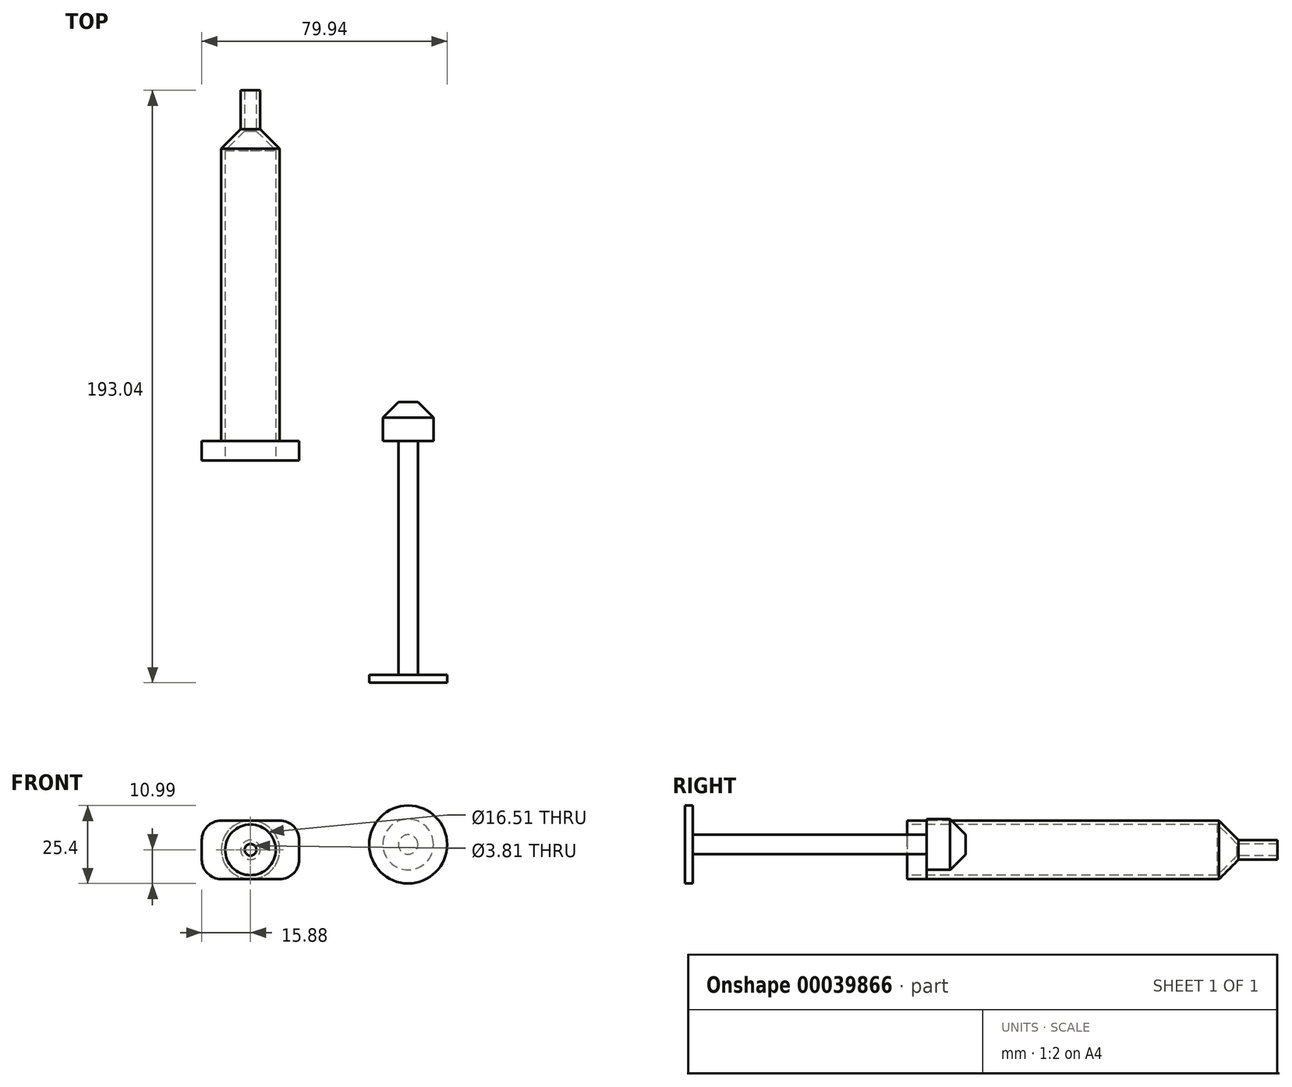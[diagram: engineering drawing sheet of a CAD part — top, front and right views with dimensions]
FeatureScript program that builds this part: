
annotation { "Feature Type Name" : "Feature", "Feature Type Description" : "" }
export const myFeature = defineFeature(function(context is Context, id is Id, definition is map)
    precondition{}
    {
        {
            var Q0;
            Q0=qCreatedBy(makeId("Front.planeOp"),FACE);
            var sketch = newSketch(context, id + "F0", { "sketchPlane" : qUnion([Q0])});
            skCircle(sketch, "E0", {"center": v(0, 0) * mm, "radius": 9.53 * mm});
            skSolve(sketch);
        }
        {
            var Q0;
            Q0 = qSketchRegion(id + "F0", true);
            extrude(context, id + "F1", {"entities" : qUnion([Q0]), "oppositeDirection" : true, "depth" : 101.6 * mm});
        }
        {
            var Q0;
            Q0=makeQuery(id+"F1.opExtrude","CAP_EDGE",EDGE,{"disambiguationData":[OSD([sQuery(id+"F0.wireOp",EDGE,"E0")])],"isStart":false});
            chamfer(context, id + "F2", {"entities" : qUnion([Q0]), "width" : 6.35 * mm, "tangentPropagation" : true});
        }
        {
            var Q0;
            Q0=makeQuery(id+"F1.opExtrude","CAP_FACE",FACE,{"disambiguationData":[OSD([sQuery(id+"F0.wireOp",EDGE,"E0")])],"isStart":false});
            extrude(context, id + "F3", {"entities" : qUnion([Q0]), "operationType" : NewBodyOperationType.ADD, "depth" : 12.7 * mm});
        }
        {
            var Q0;
            Q0=makeQuery(id+"F1.opExtrude","CAP_FACE",FACE,{"disambiguationData":[OSD([sQuery(id+"F0.wireOp",EDGE,"E0")])],"isStart":true});
            shell(context, id + "F4", {"entities" : qUnion([Q0]), "thickness" : 1.27 * mm});
        }
        {
            var Q0;
            {var subQ0=sQuery(id+"F0.wireOp",EDGE,"E0");Q0=makeQuery(id+"F4.opShell","OFFSET_FACE",FACE,{"disambiguationData":[OSD([subQ0]),TDD([makeQuery(id+"F3.opExtrude","CAP_FACE",FACE,{"disambiguationData":[OSD([subQ0])],"isStart":false})])]});}
            extrude(context, id + "F5", {"entities" : qUnion([Q0]), "operationType" : NewBodyOperationType.REMOVE, "oppositeDirection" : true, "depth" : 25.4 * mm});
        }
        {
            var Q0;
            Q0=makeQuery(id+"F1.opExtrude","CAP_FACE",FACE,{"disambiguationData":[OSD([sQuery(id+"F0.wireOp",EDGE,"E0")])],"isStart":true});
            var sketch = newSketch(context, id + "F6", { "sketchPlane" : qUnion([Q0])});
            skLineSegment(sketch, "E1.rect.bottom", {"start": v(-15.88, 9.52) * mm, "end": v(15.88, 9.52) * mm});
            skLineSegment(sketch, "E1.rect.top", {"start": v(-15.88, -9.53) * mm, "end": v(15.88, -9.53) * mm});
            skLineSegment(sketch, "E1.rect.left", {"start": v(-15.88, 9.52) * mm, "end": v(-15.88, -9.53) * mm});
            skLineSegment(sketch, "E1.rect.right", {"start": v(15.88, 9.52) * mm, "end": v(15.88, -9.53) * mm});
            skPoint(sketch, "E1.rect.middle", {"position": v(0, 0) * mm});
            skSolve(sketch);
        }
        {
            var Q0;
            {var subQ5=sQuery(id+"F6.wireOp",EDGE,"E1.rect.left");Q0=makeQuery(id+"F6.imprint","IMPRINT",FACE,{"disambiguationData":[TD([[makeQuery(id+"F6.imprint","IMPRINT",EDGE,{"derivedFrom":subQ5}),1.0]])]});}
            var Q1;
            {var subQ5=sQuery(id+"F6.wireOp",EDGE,"E1.rect.right");Q1=makeQuery(id+"F6.imprint","IMPRINT",FACE,{"disambiguationData":[TD([[makeQuery(id+"F6.imprint","IMPRINT",EDGE,{"derivedFrom":subQ5}),-1.0]])]});}
            var Q2;
            {var subQ0=sQuery(id+"F0.wireOp",EDGE,"E0");var subQ1=makeQuery(id+"F1.opExtrude","CAP_EDGE",EDGE,{"disambiguationData":[OSD([subQ0])],"isStart":true});Q2=makeQuery(id+"F6.imprint","IMPRINT",FACE,{"disambiguationData":[TD([[makeQuery(id+"F6.imprint","IMPRINT",EDGE,{"derivedFrom":makeQuery(id+"F4.opShell","OFFSET_EDGE",EDGE,{"disambiguationData":[OSD([subQ0]),TDD([subQ1])]})}),-1.0]])]});}
            extrude(context, id + "F7", {"entities" : qUnion([Q0, Q1, Q2]), "operationType" : NewBodyOperationType.ADD, "depth" : 6.35 * mm});
        }
        {
            var Q0;
            Q0=makeQuery(id+"F7.opExtrude","SWEPT_EDGE",EDGE,{"disambiguationData":[OSD([sQuery(id+"F6.wireOp",EDGE,"E1.rect.bottom"),sQuery(id+"F6.wireOp",EDGE,"E1.rect.left")])]});
            var Q1;
            Q1=makeQuery(id+"F7.opExtrude","SWEPT_EDGE",EDGE,{"disambiguationData":[OSD([sQuery(id+"F6.wireOp",EDGE,"E1.rect.bottom"),sQuery(id+"F6.wireOp",EDGE,"E1.rect.right")])]});
            var Q2;
            Q2=makeQuery(id+"F7.opExtrude","SWEPT_EDGE",EDGE,{"disambiguationData":[OSD([sQuery(id+"F6.wireOp",EDGE,"E1.rect.top"),sQuery(id+"F6.wireOp",EDGE,"E1.rect.left")])]});
            var Q3;
            Q3=makeQuery(id+"F7.opExtrude","SWEPT_EDGE",EDGE,{"disambiguationData":[OSD([sQuery(id+"F6.wireOp",EDGE,"E1.rect.top"),sQuery(id+"F6.wireOp",EDGE,"E1.rect.right")])]});
            fillet(context, id + "F8", {"entities" : qUnion([Q0, Q1, Q2, Q3]), "radius" : 6.35 * mm, "tangentPropagation" : true, "allowEdgeOverflow" : false});
        }
        {
            var Q0;
            Q0=qCreatedBy(makeId("Front.planeOp"),FACE);
            var sketch = newSketch(context, id + "F9", { "sketchPlane" : qUnion([Q0])});
            skCircle(sketch, "E2", {"center": v(51.36, 1.71) * mm, "radius": 8.26 * mm});
            skSolve(sketch);
        }
        {
            var Q0;
            Q0=makeQuery(id+"F9.imprint","IMPRINT",FACE,{"disambiguationData":[TD([[makeQuery(id+"F9.imprint","IMPRINT",EDGE,{"derivedFrom":sQuery(id+"F9.wireOp",EDGE,"E2")}),1.0]])]});
            extrude(context, id + "F10", {"entities" : qUnion([Q0]), "oppositeDirection" : true, "depth" : 12.7 * mm});
        }
        {
            var Q0;
            Q0=makeQuery(id+"F10.opExtrude","CAP_FACE",FACE,{"disambiguationData":[OSD([sQuery(id+"F9.wireOp",EDGE,"E2")])],"isStart":true});
            var sketch = newSketch(context, id + "F11", { "sketchPlane" : qUnion([Q0])});
            skCircle(sketch, "E3", {"center": v(51.36, 1.71) * mm, "radius": 3.18 * mm});
            skSolve(sketch);
        }
        {
            var Q0;
            Q0 = qSketchRegion(id + "F11", true);
            extrude(context, id + "F12", {"entities" : qUnion([Q0]), "operationType" : NewBodyOperationType.ADD, "depth" : 76.2 * mm});
        }
        {
            var Q0;
            Q0=makeQuery(id+"F12.opExtrude","CAP_FACE",FACE,{"disambiguationData":[OSD([sQuery(id+"F11.wireOp",EDGE,"E3")])],"isStart":false});
            var sketch = newSketch(context, id + "F13", { "sketchPlane" : qUnion([Q0])});
            skCircle(sketch, "E4", {"center": v(51.36, 1.71) * mm, "radius": 12.7 * mm});
            skSolve(sketch);
        }
        {
            var Q0;
            Q0 = qSketchRegion(id + "F13", true);
            extrude(context, id + "F14", {"entities" : qUnion([Q0]), "operationType" : NewBodyOperationType.ADD, "depth" : 2.54 * mm});
        }
        {
            var Q0;
            Q0=makeQuery(id+"F10.opExtrude","CAP_FACE",FACE,{"disambiguationData":[OSD([sQuery(id+"F9.wireOp",EDGE,"E2")])],"isStart":false});
            chamfer(context, id + "F15", {"entities" : qUnion([Q0]), "width" : 5.08 * mm, "tangentPropagation" : true});
        }
    });
